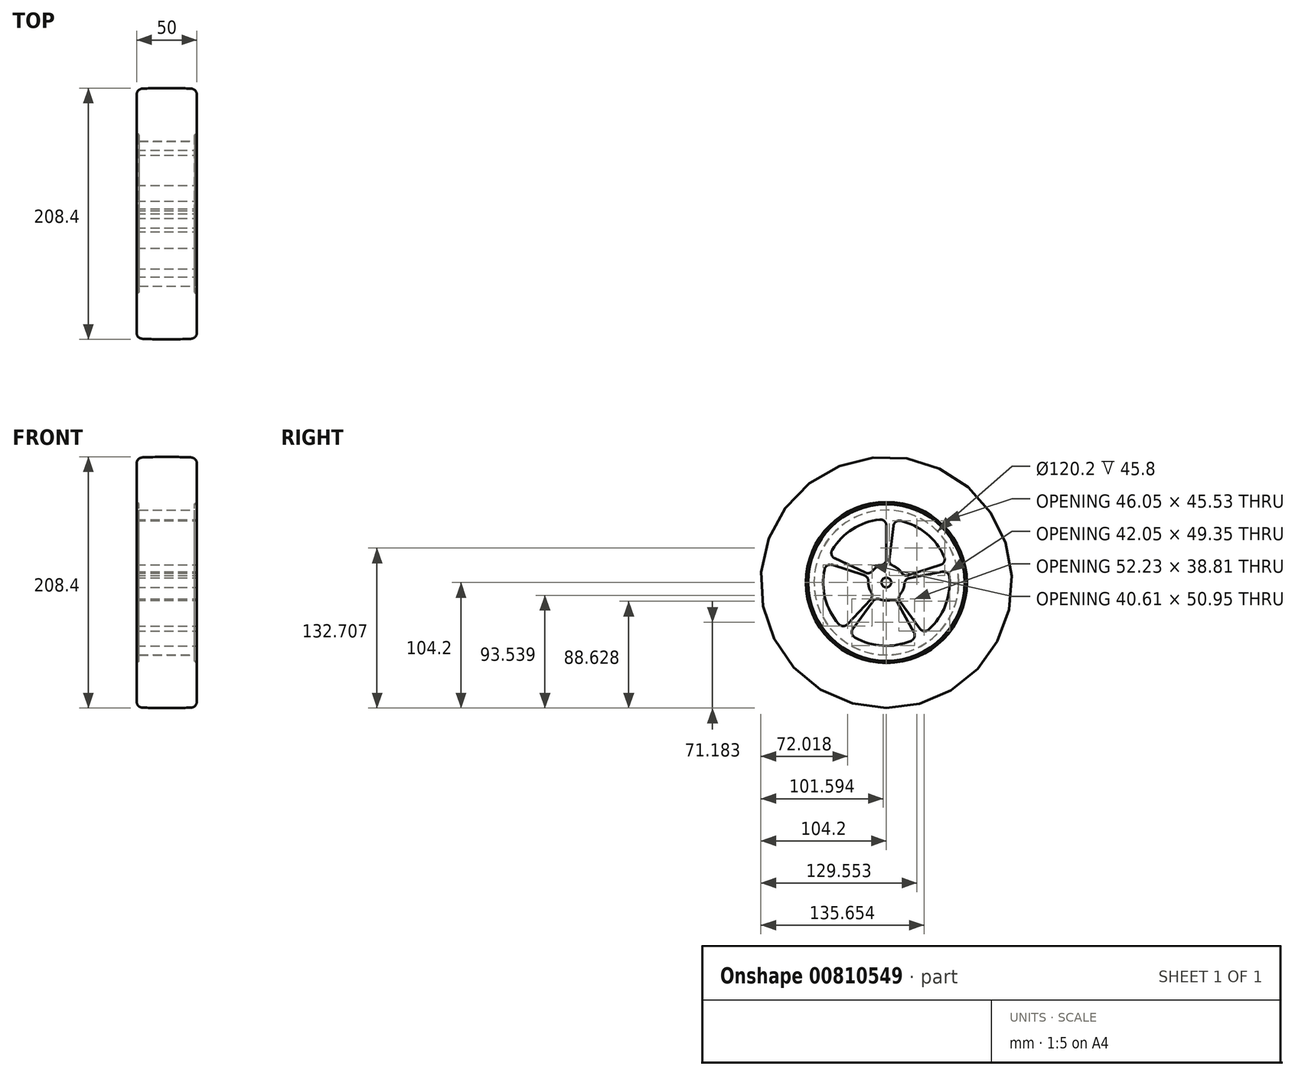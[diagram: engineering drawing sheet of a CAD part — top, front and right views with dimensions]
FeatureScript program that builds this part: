
annotation { "Feature Type Name" : "Feature", "Feature Type Description" : "" }
export const myFeature = defineFeature(function(context is Context, id is Id, definition is map)
    precondition{}
    {
        {
            var Q0;
            Q0=qCreatedBy(makeId("Front.planeOp"),FACE);
            var sketch = newSketch(context, id + "F0", { "sketchPlane" : qUnion([Q0])});
            skLineSegment(sketch, "E0", {"start": v(0, 0) * mm, "end": v(0, 104.2) * mm, "construction": true});
            skLineSegment(sketch, "E1", {"start": v(132.94, 0) * mm, "end": v(-109, 0) * mm, "construction": true});
            skLineSegment(sketch, "E2", {"start": v(0, 0) * mm, "end": v(25, 0) * mm});
            skLineSegment(sketch, "E3", {"start": v(25, 0) * mm, "end": v(25, 65) * mm});
            skLineSegment(sketch, "E4", {"start": v(25, 65) * mm, "end": v(23, 65) * mm});
            skLineSegment(sketch, "E5", {"start": v(23, 65) * mm, "end": v(23, 60) * mm});
            skLineSegment(sketch, "E6", {"start": v(23, 60) * mm, "end": v(0, 60) * mm});
            skLineSegment(sketch, "E7.MirrorCS", {"start": v(-23, 60) * mm, "end": v(0, 60) * mm});
            skLineSegment(sketch, "E8.MirrorCS", {"start": v(-23, 65) * mm, "end": v(-23, 60) * mm});
            skLineSegment(sketch, "E9.MirrorCS", {"start": v(-25, 65) * mm, "end": v(-23, 65) * mm});
            skLineSegment(sketch, "E10.MirrorCS", {"start": v(-25, 0) * mm, "end": v(-25, 65) * mm});
            skLineSegment(sketch, "E11.MirrorCS", {"start": v(0, 0) * mm, "end": v(-25, 0) * mm});
            skSolve(sketch);
        }
        {
            var Q0;
            Q0 = qSketchRegion(id + "F0", true);
            var Q1;
            Q1=sQuery(id+"F0.wireOp",EDGE,"E1");
            revolve(context, id + "F1", {"surfaceOperationType" : NewSurfaceOperationType.NEW, "entities" : qUnion([Q0]), "axis" : qUnion([Q1]), "revolveType" : RevolveType.FULL});
        }
        {
            var Q0;
            Q0=makeQuery(id+"F1.opRevolve","SWEPT_FACE",FACE,{"disambiguationData":[OSD([sQuery(id+"F0.wireOp",EDGE,"E3")])]});
            var sketch = newSketch(context, id + "F2", { "sketchPlane" : qUnion([Q0])});
            skPoint(sketch, "E12", {"position": v(0, 0) * mm});
            skArc(sketch, "E13", {"start": v(-14.97, 0.92) * mm, "mid": v(-14.52, -3.76) * mm, "end": v(-12.65, -8.06) * mm});
            skArc(sketch, "E14", {"start": v(-5.53, 52.2) * mm, "mid": v(-28.2, 44.28) * mm, "end": v(-44.98, 27.07) * mm});
            skLineSegment(sketch, "E15", {"start": v(0, 19.36) * mm, "end": v(0, 47.24) * mm});
            skLineSegment(sketch, "E16.1.0", {"start": v(2.36, 19.22) * mm, "end": v(5.76, 46.88) * mm});
            skLineSegment(sketch, "E16.anchor1", {"start": v(0, 0) * mm, "end": v(0, 15) * mm, "construction": true});
            skLineSegment(sketch, "E16.anchor2", {"start": v(0, 0) * mm, "end": v(1.83, 14.89) * mm, "construction": true});
            skLineSegment(sketch, "E17.1.0", {"start": v(-17.55, 8.18) * mm, "end": v(-42.81, 19.96) * mm});
            skLineSegment(sketch, "E17.1.1", {"start": v(-18.42, 5.98) * mm, "end": v(-44.92, 14.6) * mm});
            skLineSegment(sketch, "E17.2.0", {"start": v(-13.2, -14.16) * mm, "end": v(-32.21, -34.55) * mm});
            skLineSegment(sketch, "E17.2.1", {"start": v(-11.38, -15.67) * mm, "end": v(-27.76, -38.21) * mm});
            skLineSegment(sketch, "E17.3.0", {"start": v(9.39, -16.94) * mm, "end": v(22.9, -41.31) * mm});
            skLineSegment(sketch, "E17.3.1", {"start": v(11.38, -15.67) * mm, "end": v(27.76, -38.21) * mm});
            skLineSegment(sketch, "E17.4.0", {"start": v(19, 3.7) * mm, "end": v(46.37, 9.01) * mm});
            skLineSegment(sketch, "E17.4.1", {"start": v(18.42, 5.98) * mm, "end": v(44.92, 14.6) * mm});
            skArc(sketch, "E18.trimOffspring", {"start": v(-51.36, 10.88) * mm, "mid": v(-50.83, -13.14) * mm, "end": v(-39.65, -34.41) * mm});
            skArc(sketch, "E19.trimOffspring", {"start": v(-26.22, -45.49) * mm, "mid": v(-3.2, -52.4) * mm, "end": v(20.48, -48.34) * mm});
            skArc(sketch, "E20.trimOffspring", {"start": v(35.16, -38.99) * mm, "mid": v(48.85, -19.24) * mm, "end": v(52.3, 4.54) * mm});
            skArc(sketch, "E21.trimOffspring", {"start": v(47.95, 21.39) * mm, "mid": v(33.4, 40.51) * mm, "end": v(11.85, 51.15) * mm});
            skArc(sketch, "E22.trimOffspring", {"start": v(12.65, 8.05) * mm, "mid": v(9.54, 11.57) * mm, "end": v(5.5, 13.96) * mm});
            skArc(sketch, "E23.trimOffspring", {"start": v(11.57, -9.55) * mm, "mid": v(13.96, -5.5) * mm, "end": v(14.97, -0.9) * mm});
            skArc(sketch, "E24.trimOffspring", {"start": v(-5.5, -13.95) * mm, "mid": v(-0.92, -14.97) * mm, "end": v(3.76, -14.52) * mm});
            skArc(sketch, "E25.trimOffspring", {"start": v(-3.75, 14.52) * mm, "mid": v(-8.06, 12.65) * mm, "end": v(-11.58, 9.54) * mm});
            skPoint(sketch, "E26.visualSharp", {"position": v(0, 52.5) * mm});
            skArc(sketch, "E26.filletArc", {"start": v(0, 47.24) * mm, "mid": v(-1.66, 50.95) * mm, "end": v(-5.53, 52.2) * mm});
            skPoint(sketch, "E27.visualSharp", {"position": v(-47.58, 22.19) * mm});
            skArc(sketch, "E27.filletArc", {"start": v(-44.98, 27.07) * mm, "mid": v(-45.48, 23.03) * mm, "end": v(-42.81, 19.96) * mm});
            skPoint(sketch, "E28.visualSharp", {"position": v(-49.93, 16.22) * mm});
            skArc(sketch, "E28.filletArc", {"start": v(-44.92, 14.6) * mm, "mid": v(-48.97, 14.17) * mm, "end": v(-51.36, 10.88) * mm});
            skPoint(sketch, "E29.visualSharp", {"position": v(-35.8, -38.4) * mm});
            skArc(sketch, "E29.filletArc", {"start": v(-39.65, -34.41) * mm, "mid": v(-35.96, -36.14) * mm, "end": v(-32.21, -34.55) * mm});
            skPoint(sketch, "E30.visualSharp", {"position": v(-30.86, -42.47) * mm});
            skArc(sketch, "E30.filletArc", {"start": v(-27.76, -38.21) * mm, "mid": v(-28.6, -42.2) * mm, "end": v(-26.22, -45.49) * mm});
            skPoint(sketch, "E31.visualSharp", {"position": v(25.45, -45.92) * mm});
            skArc(sketch, "E31.filletArc", {"start": v(20.48, -48.34) * mm, "mid": v(23.25, -45.37) * mm, "end": v(22.9, -41.31) * mm});
            skPoint(sketch, "E32.visualSharp", {"position": v(30.86, -42.47) * mm});
            skArc(sketch, "E32.filletArc", {"start": v(27.76, -38.21) * mm, "mid": v(31.29, -40.25) * mm, "end": v(35.16, -38.99) * mm});
            skPoint(sketch, "E33.visualSharp", {"position": v(51.54, 10.02) * mm});
            skArc(sketch, "E33.filletArc", {"start": v(52.3, 4.54) * mm, "mid": v(50.33, 8.1) * mm, "end": v(46.37, 9.01) * mm});
            skPoint(sketch, "E34.visualSharp", {"position": v(49.93, 16.22) * mm});
            skArc(sketch, "E34.filletArc", {"start": v(44.92, 14.6) * mm, "mid": v(47.95, 17.32) * mm, "end": v(47.95, 21.39) * mm});
            skPoint(sketch, "E35.visualSharp", {"position": v(6.4, 52.1) * mm});
            skArc(sketch, "E35.filletArc", {"start": v(11.85, 51.15) * mm, "mid": v(7.85, 50.37) * mm, "end": v(5.76, 46.88) * mm});
            skPoint(sketch, "E36.visualSharp", {"position": v(14.72, 2.86) * mm});
            skArc(sketch, "E36.filletArc", {"start": v(19, 3.7) * mm, "mid": v(16.2, 2.08) * mm, "end": v(14.97, -0.9) * mm});
            skPoint(sketch, "E37.visualSharp", {"position": v(8.82, -12.14) * mm});
            skArc(sketch, "E37.filletArc", {"start": v(11.57, -9.55) * mm, "mid": v(10.43, -12.57) * mm, "end": v(11.38, -15.67) * mm});
            skPoint(sketch, "E38.visualSharp", {"position": v(7.27, -13.12) * mm});
            skArc(sketch, "E38.filletArc", {"start": v(9.39, -16.94) * mm, "mid": v(6.99, -14.77) * mm, "end": v(3.76, -14.52) * mm});
            skPoint(sketch, "E39.visualSharp", {"position": v(-8.82, -12.14) * mm});
            skArc(sketch, "E39.filletArc", {"start": v(-5.5, -13.95) * mm, "mid": v(-8.74, -13.8) * mm, "end": v(-11.38, -15.67) * mm});
            skPoint(sketch, "E40.visualSharp", {"position": v(-10.23, -10.97) * mm});
            skArc(sketch, "E40.filletArc", {"start": v(-13.2, -14.16) * mm, "mid": v(-11.88, -11.2) * mm, "end": v(-12.65, -8.06) * mm});
            skPoint(sketch, "E41.visualSharp", {"position": v(-14.27, 4.64) * mm});
            skArc(sketch, "E41.filletArc", {"start": v(-14.97, 0.92) * mm, "mid": v(-15.83, 4.04) * mm, "end": v(-18.42, 5.98) * mm});
            skPoint(sketch, "E42.visualSharp", {"position": v(-13.6, 6.34) * mm});
            skArc(sketch, "E42.filletArc", {"start": v(-17.55, 8.18) * mm, "mid": v(-14.33, 7.84) * mm, "end": v(-11.58, 9.54) * mm});
            skPoint(sketch, "E43.visualSharp", {"position": v(0, 15) * mm});
            skArc(sketch, "E43.filletArc", {"start": v(-3.75, 14.52) * mm, "mid": v(-1.05, 16.3) * mm, "end": v(0, 19.36) * mm});
            skPoint(sketch, "E44.visualSharp", {"position": v(1.83, 14.89) * mm});
            skArc(sketch, "E44.filletArc", {"start": v(2.36, 19.22) * mm, "mid": v(3.03, 16.05) * mm, "end": v(5.5, 13.96) * mm});
            skPoint(sketch, "E45.visualSharp", {"position": v(14.27, 4.64) * mm});
            skArc(sketch, "E45.filletArc", {"start": v(12.65, 8.05) * mm, "mid": v(15.18, 6.03) * mm, "end": v(18.42, 5.98) * mm});
            skSolve(sketch);
        }
        {
            var Q0;
            Q0 = qSketchRegion(id + "F2", true);
            extrude(context, id + "F3", {"entities" : qUnion([Q0]), "operationType" : NewBodyOperationType.REMOVE, "endBound" : BoundingType.THROUGH_ALL, "oppositeDirection" : true, "depth" : 25 * mm, "offsetDistance" : 25 * mm});
        }
        {
            var Q0;
            Q0=makeQuery(id+"F1.opRevolve","SWEPT_FACE",FACE,{"disambiguationData":[OSD([sQuery(id+"F0.wireOp",EDGE,"E3")])]});
            var sketch = newSketch(context, id + "F4", { "sketchPlane" : qUnion([Q0])});
            skCircle(sketch, "E46", {"center": v(0, 0) * mm, "radius": 4 * mm});
            skSolve(sketch);
        }
        {
            var Q0;
            Q0=makeQuery(id+"F4.imprint","IMPRINT",FACE,{"disambiguationData":[TD([[makeQuery(id+"F4.imprint","IMPRINT",EDGE,{"derivedFrom":sQuery(id+"F4.wireOp",EDGE,"E46")}),1.0]])]});
            extrude(context, id + "F5", {"entities" : qUnion([Q0]), "operationType" : NewBodyOperationType.REMOVE, "endBound" : BoundingType.THROUGH_ALL, "oppositeDirection" : true, "depth" : 25 * mm, "offsetDistance" : 25 * mm});
        }
        {
            var Q0;
            Q0=qCreatedBy(makeId("Front.planeOp"),FACE);
            var sketch = newSketch(context, id + "F6", { "sketchPlane" : qUnion([Q0])});
            skLineSegment(sketch, "E47", {"start": v(-22.9, 60.1) * mm, "end": v(0, 60.1) * mm});
            skLineSegment(sketch, "E48.MirrorCS", {"start": v(22.9, 60.1) * mm, "end": v(0, 60.1) * mm});
            skLineSegment(sketch, "E49", {"start": v(-22.9, 60.1) * mm, "end": v(-22.9, 65.2) * mm});
            skLineSegment(sketch, "E50", {"start": v(25, 66.77) * mm, "end": v(25, 98.76) * mm});
            skLineSegment(sketch, "E51.MirrorCS", {"start": v(-25, 66.77) * mm, "end": v(-25, 98.76) * mm});
            skArc(sketch, "E52", {"start": v(20.22, 103.75) * mm, "mid": v(0, 104.2) * mm, "end": v(-20.22, 103.75) * mm});
            skPoint(sketch, "E53.visualSharp", {"position": v(25, 103.51) * mm});
            skArc(sketch, "E53.filletArc", {"start": v(25, 98.76) * mm, "mid": v(23.61, 102.21) * mm, "end": v(20.22, 103.75) * mm});
            skPoint(sketch, "E54.visualSharp", {"position": v(-25, 103.51) * mm});
            skArc(sketch, "E54.filletArc", {"start": v(-20.22, 103.75) * mm, "mid": v(-23.61, 102.21) * mm, "end": v(-25, 98.76) * mm});
            skLineSegment(sketch, "E55.MirrorCS", {"start": v(22.9, 60.1) * mm, "end": v(22.9, 65.2) * mm});
            skLineSegment(sketch, "E56", {"start": v(-25, 66.77) * mm, "end": v(-22.9, 65.2) * mm});
            skLineSegment(sketch, "E57.MirrorCS", {"start": v(25, 66.77) * mm, "end": v(22.9, 65.2) * mm});
            skSolve(sketch);
        }
        {
            var Q0;
            Q0=makeQuery(id+"F6.imprint","IMPRINT",FACE,{"disambiguationData":[TD([[makeQuery(id+"F6.imprint","IMPRINT",EDGE,{"derivedFrom":sQuery(id+"F6.wireOp",EDGE,"E47")}),1.0]])]});
            var Q1;
            Q1=sQuery(id+"F0.wireOp",EDGE,"E1");
            revolve(context, id + "F7", {"surfaceOperationType" : NewSurfaceOperationType.NEW, "entities" : qUnion([Q0]), "axis" : qUnion([Q1]), "revolveType" : RevolveType.FULL});
        }
    });
